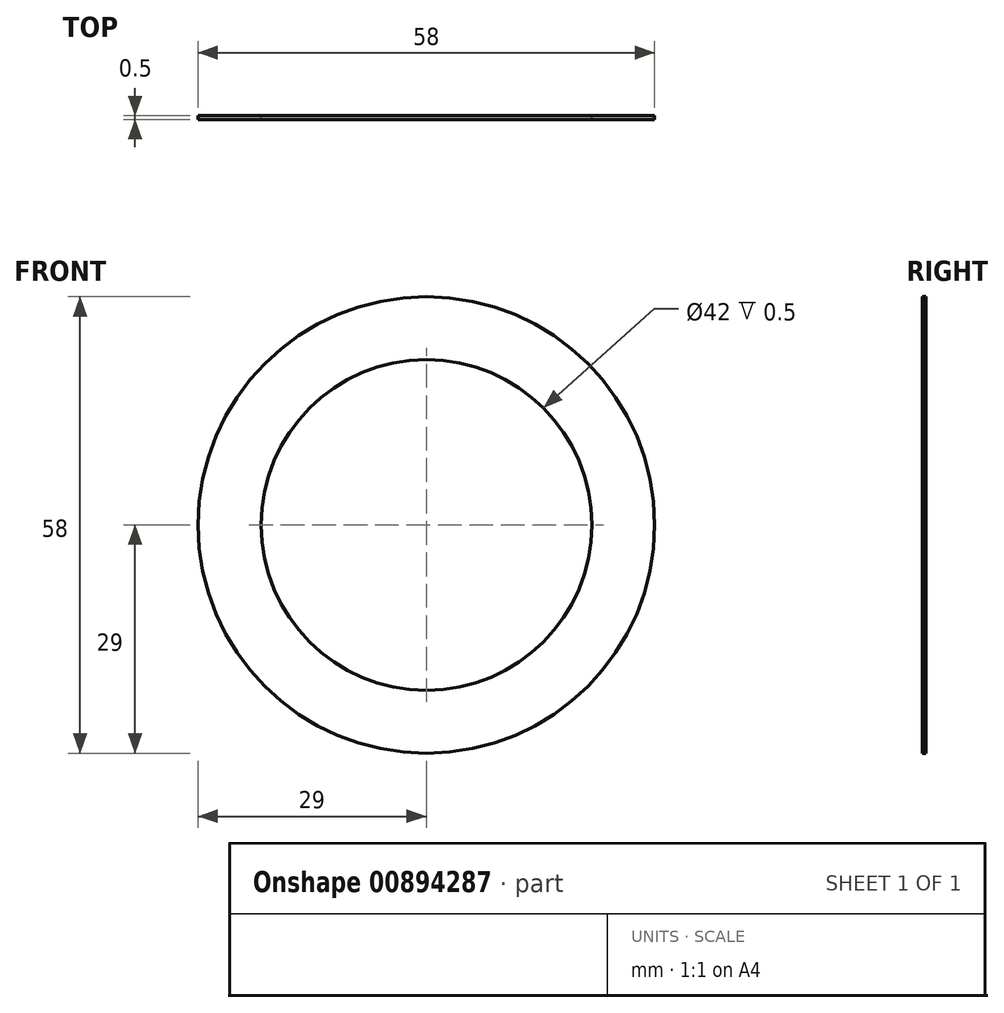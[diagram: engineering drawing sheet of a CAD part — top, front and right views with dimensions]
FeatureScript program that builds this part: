
annotation { "Feature Type Name" : "Feature", "Feature Type Description" : "" }
export const myFeature = defineFeature(function(context is Context, id is Id, definition is map)
    precondition{}
    {
        {
            var Q0;
            Q0=qCreatedBy(makeId("Front.planeOp"),FACE);
            var sketch = newSketch(context, id + "F0", { "sketchPlane" : qUnion([Q0])});
            skCircle(sketch, "E0", {"center": v(0, 0) * mm, "radius": 21 * mm});
            skCircle(sketch, "E1", {"center": v(0, 0) * mm, "radius": 29 * mm});
            skSolve(sketch);
        }
        {
            var Q0;
            Q0=makeQuery(id+"F0.imprint","IMPRINT",FACE,{"disambiguationData":[TD([[makeQuery(id+"F0.imprint","IMPRINT",EDGE,{"derivedFrom":sQuery(id+"F0.wireOp",EDGE,"E0")}),-1.0]])]});
            extrude(context, id + "F1", {"entities" : qUnion([Q0]), "depth" : 0.5 * mm, "offsetDistance" : 25 * mm});
        }
    });
